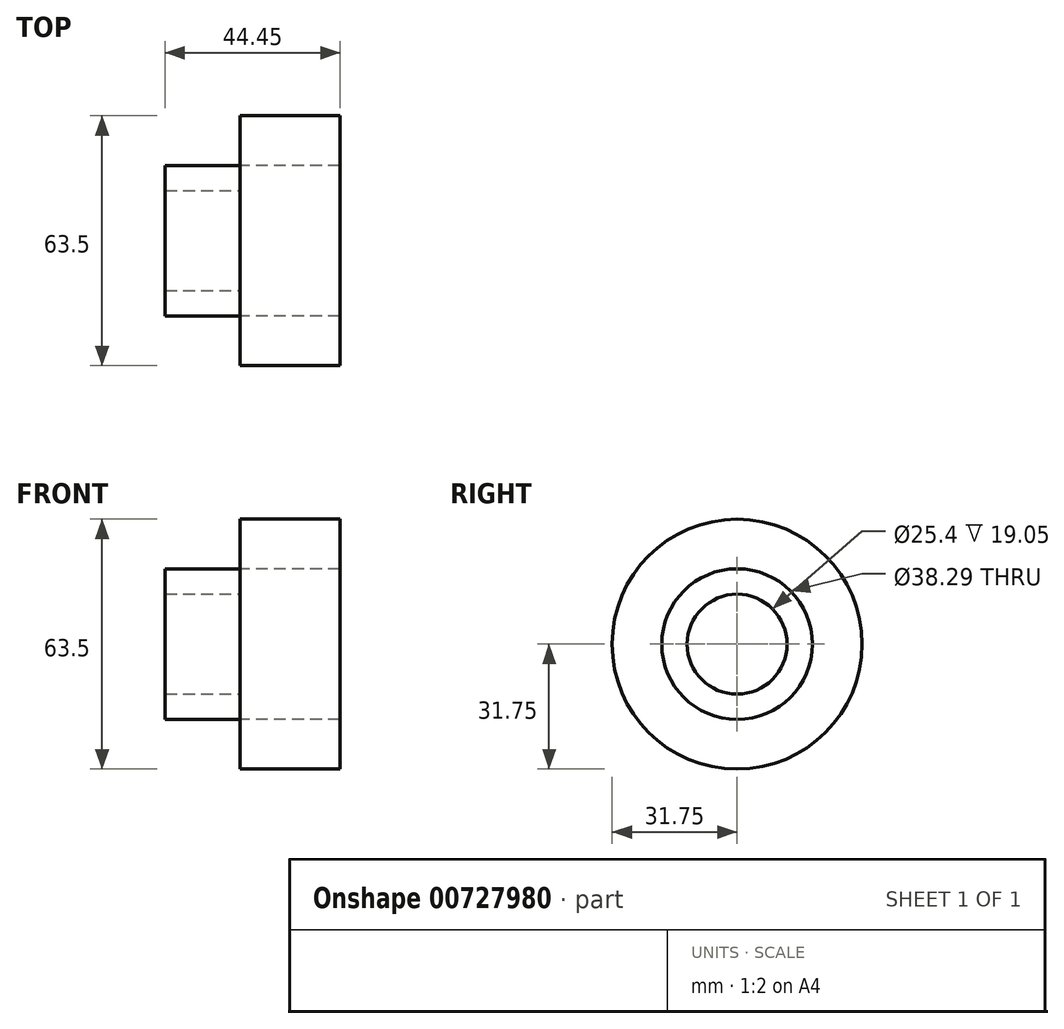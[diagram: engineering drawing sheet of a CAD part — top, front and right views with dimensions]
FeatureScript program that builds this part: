
annotation { "Feature Type Name" : "Feature", "Feature Type Description" : "" }
export const myFeature = defineFeature(function(context is Context, id is Id, definition is map)
    precondition{}
    {
        {
            var Q0;
            Q0=qCreatedBy(makeId("Right.planeOp"),FACE);
            var sketch = newSketch(context, id + "F0", { "sketchPlane" : qUnion([Q0])});
            skCircle(sketch, "E0", {"center": v(0, 0) * mm, "radius": 31.75 * mm});
            skPoint(sketch, "E1.orphan", {"position": v(-31.75, 0) * mm});
            skCircle(sketch, "E2", {"center": v(0, 0) * mm, "radius": 19.14 * mm});
            skPoint(sketch, "E3.orphan", {"position": v(-19.14, 0) * mm});
            skCircle(sketch, "E4", {"center": v(0, 0) * mm, "radius": 12.7 * mm});
            skPoint(sketch, "E5.orphan", {"position": v(-12.7, 0) * mm});
            skSolve(sketch);
        }
        {
            var Q0;
            Q0=makeQuery(id+"F0.imprint","IMPRINT",FACE,{"disambiguationData":[TD([[makeQuery(id+"F0.imprint","IMPRINT",EDGE,{"derivedFrom":sQuery(id+"F0.wireOp",EDGE,"E0")}),1.0]])]});
            extrude(context, id + "F1", {"entities" : qUnion([Q0]), "depth" : 25.4 * mm, "offsetDistance" : 25.4 * mm});
        }
        {
            var Q0;
            Q0=makeQuery(id+"F0.imprint","IMPRINT",FACE,{"disambiguationData":[TD([[makeQuery(id+"F0.imprint","IMPRINT",EDGE,{"derivedFrom":sQuery(id+"F0.wireOp",EDGE,"E2")}),1.0]])]});
            extrude(context, id + "F2", {"entities" : qUnion([Q0]), "oppositeDirection" : true, "depth" : 19.05 * mm, "offsetDistance" : 25.4 * mm});
        }
    });
